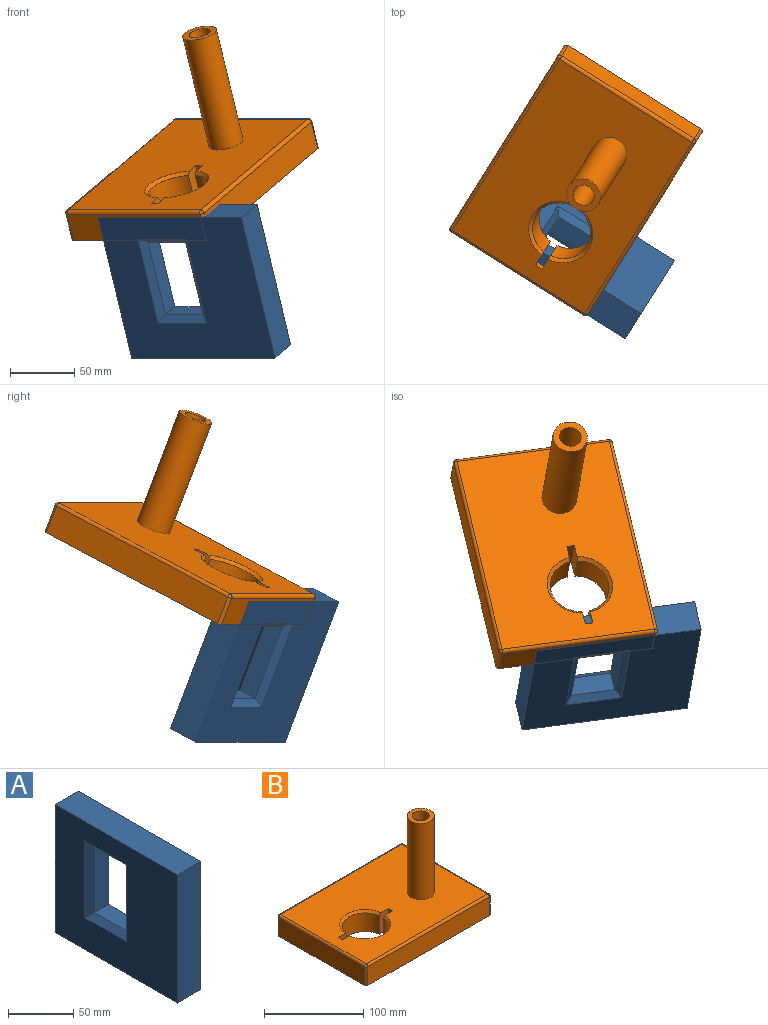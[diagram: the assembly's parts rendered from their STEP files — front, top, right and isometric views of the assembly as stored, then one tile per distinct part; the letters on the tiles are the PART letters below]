
ASSEMBLY  parts=2 mates=1
PART A: 18 faces, bbox 25.4x132x119.9 mm
  f0: plane 132x119.89mm, normal (1,0,0), area 12605.5mm2, adj f2,f3,f4,f5,f14,f15,f16,f17
  f1: plane 132x119.89mm, normal (-1,0,0), area 12605.5mm2, adj f2,f3,f4,f5,f10,f11,f12,f13
  f2: plane 119.89x25.4mm, normal (0,1,0), area 3045.2mm2, adj f0,f1,f4,f5
  f3: plane 119.89x25.4mm, normal (0,-1,0), area 3045.2mm2, adj f0,f1,f4,f5
  f4: plane 132x25.4mm, normal (0,0,1), area 3352.8mm2, adj f0,f1,f2,f3
  f5: plane 132x25.4mm, normal (0,0,-1), area 3352.8mm2, adj f0,f1,f2,f3
  f6: plane 34.55x15.24mm, normal (0,0,-1), area 526.6mm2, adj f7,f9,f10,f16
  f7: plane 61.85x15.24mm, normal (0,-1,0), area 942.6mm2, adj f6,f8,f11,f17
  f8: plane 34.55x15.24mm, normal (0,0,1), area 526.6mm2, adj f7,f9,f13,f15
  f9: plane 61.85x15.24mm, normal (0,1,0), area 942.6mm2, adj f6,f8,f12,f14
  f10: plane 44.71x5.08mm, normal (-0.71,0,-0.71), area 284.7mm2, adj f1,f6,f11,f12
  f11: plane 72.01x5.08mm, normal (-0.71,-0.71,0), area 480.8mm2, adj f1,f7,f10,f13
  f12: plane 72.01x5.08mm, normal (-0.71,0.71,0), area 480.8mm2, adj f1,f9,f10,f13
  f13: plane 44.71x5.08mm, normal (-0.71,0,0.71), area 284.7mm2, adj f1,f8,f11,f12
  f14: plane 72.01x5.08mm, normal (0.71,0.71,0), area 480.8mm2, adj f0,f9,f15,f16
  f15: plane 44.71x5.08mm, normal (0.71,0,0.71), area 284.7mm2, adj f0,f8,f14,f17
  f16: plane 44.71x5.08mm, normal (0.71,0,-0.71), area 284.7mm2, adj f0,f6,f14,f17
  f17: plane 72.01x5.08mm, normal (0.71,-0.71,0), area 480.8mm2, adj f0,f7,f15,f16
PART B: 32 faces, bbox 177.8x127x119.4 mm
  f0: plane 172.72x22.86mm, normal (0,1,0), area 3948.4mm2, adj f13,f18,f24,f27
  f1: plane 121.92x22.86mm, normal (-1,0,0), area 2787.1mm2, adj f13,f21,f25,f27
  f2: plane 172.72x22.86mm, normal (0,-1,0), area 3948.4mm2, adj f13,f16,f20,f21
  f3: cylinder r=23.14mm len=45.87mm, axis (0,0,-1), area 1521.7mm2, adj f4,f10,f13,f14
  f4: plane 25.42x12.64mm, normal (0,1,0), area 317.4mm2, adj f3,f5,f12,f13,f14
  f5: plane 25.4x6.1mm, normal (1,0,0), area 155mm2, adj f4,f6,f12,f13
  f6: plane 25.42x12.64mm, normal (0,-1,0), area 317.4mm2, adj f5,f7,f12,f13,f15
  f7: cylinder r=23.14mm len=45.87mm, axis (0,0,-1), area 1521.7mm2, adj f6,f8,f13,f15
  f8: plane 25.42x12.64mm, normal (0,-1,0), area 317.4mm2, adj f7,f9,f12,f13,f15
  f9: plane 25.4x6.1mm, normal (-1,0,0), area 155mm2, adj f8,f10,f12,f13
  f10: plane 25.42x12.64mm, normal (0,1,0), area 317.4mm2, adj f3,f9,f12,f13,f14
  f11: plane 121.92x22.86mm, normal (1,0,0), area 2787.1mm2, adj f13,f16,f18,f19
  f12: plane 172.72x121.92mm, normal (0,0,1), area 18292.9mm2, adj f4,f5,f6,f8,f9,f10,f14,f15
  f13: plane 177.8x127mm, normal (0,0,-1), area 20740.9mm2, adj f0,f1,f2,f3,f4,f5,f6,f7
  f14: cone r=23.14mm half-angle=45deg, axis (0,0,1), area 253.4mm2, adj f3,f4,f10,f12
  f15: cone r=23.14mm half-angle=45deg, axis (0,0,1), area 253.4mm2, adj f6,f7,f8,f12
  f16: cylinder r=2.54mm len=22.86mm, axis (0,0,-1), area 91.2mm2, adj f2,f11,f13,f17
  f17: sphere r=2.54mm, area 10.1mm2, adj f16,f19,f20
  f18: cylinder r=2.54mm len=22.86mm, axis (0,0,-1), area 91.2mm2, adj f0,f11,f13,f22
  f19: cylinder r=2.54mm len=121.92mm, axis (0,-1,0), area 486.4mm2, adj f11,f12,f17,f22
  f20: cylinder r=2.54mm len=172.72mm, axis (-1,0,0), area 689.1mm2, adj f2,f12,f17,f23
  f21: cylinder r=2.54mm len=22.86mm, axis (0,0,-1), area 91.2mm2, adj f1,f2,f13,f23
  f22: sphere r=2.54mm, area 10.1mm2, adj f18,f19,f24
  f23: sphere r=2.54mm, area 10.1mm2, adj f20,f21,f25
  f24: cylinder r=2.54mm len=172.72mm, axis (1,0,0), area 689.1mm2, adj f0,f12,f22,f26
  f25: cylinder r=2.54mm len=121.92mm, axis (0,1,0), area 486.4mm2, adj f1,f12,f23,f26
  f26: sphere r=2.54mm, area 10.1mm2, adj f24,f25,f27
  f27: cylinder r=2.54mm len=22.86mm, axis (0,0,-1), area 91.2mm2, adj f0,f1,f13,f26
  f28: plane 27x27mm, normal (0,0,1), area 345.6mm2, adj f29,f30
  f29: cylinder r=13.5mm len=94mm, axis (0,0,1), area 7973.4mm2, adj f12,f28
  f30: cylinder r=8.5mm len=94mm, axis (0,0,1), area 5020.3mm2, adj f28,f31
  f31: plane 17x17mm, normal (0,0,1), area 227mm2, adj f30
PLACE A rot(axis=(0.2,-0.35,0.91),62.4deg) t=(-74.63,108.81,-66.66)mm
PLACE B rot(axis=(0.2,-0.35,0.91),62.4deg) t=(-141.42,48.09,4.04)mm
MATE planar B.f1 <-> A.f1  axis (-0.48,-0.77,-0.41) through (-171.88,25.61,0.7)mm
